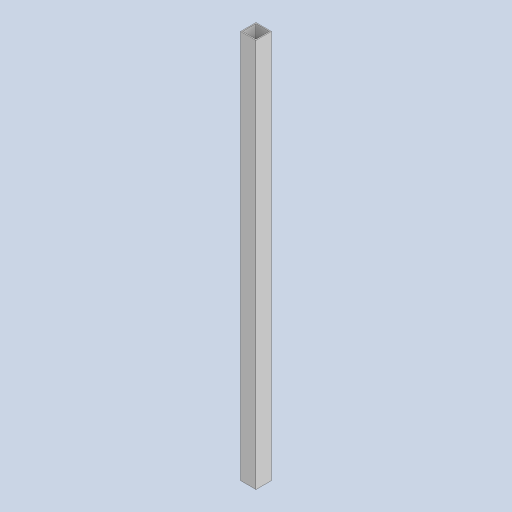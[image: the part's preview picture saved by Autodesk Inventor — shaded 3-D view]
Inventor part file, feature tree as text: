
AUTODESK INVENTOR PART (.ipt)
format: ipt  version: 2023 (Build 270158000, 158)  size: 84,992 bytes
history: native  units: mm
features: extrude x1, sketch x1
ambient origin geometry x8: Origin, YZ Plane, XZ Plane, XY Plane, X Axis, Y Axis, Z Axis, Center Point
bodies: Solid1 (feature_tree)
feature tree (2):
  extrude  "Extrusion1"  Depth=25.4mm
  sketch  "Sketch1"  dims[d0=25.4mm d1=25.4mm d2=1.5875mm d3=1.5875mm d4=640.0mm d5=0.0mm]
